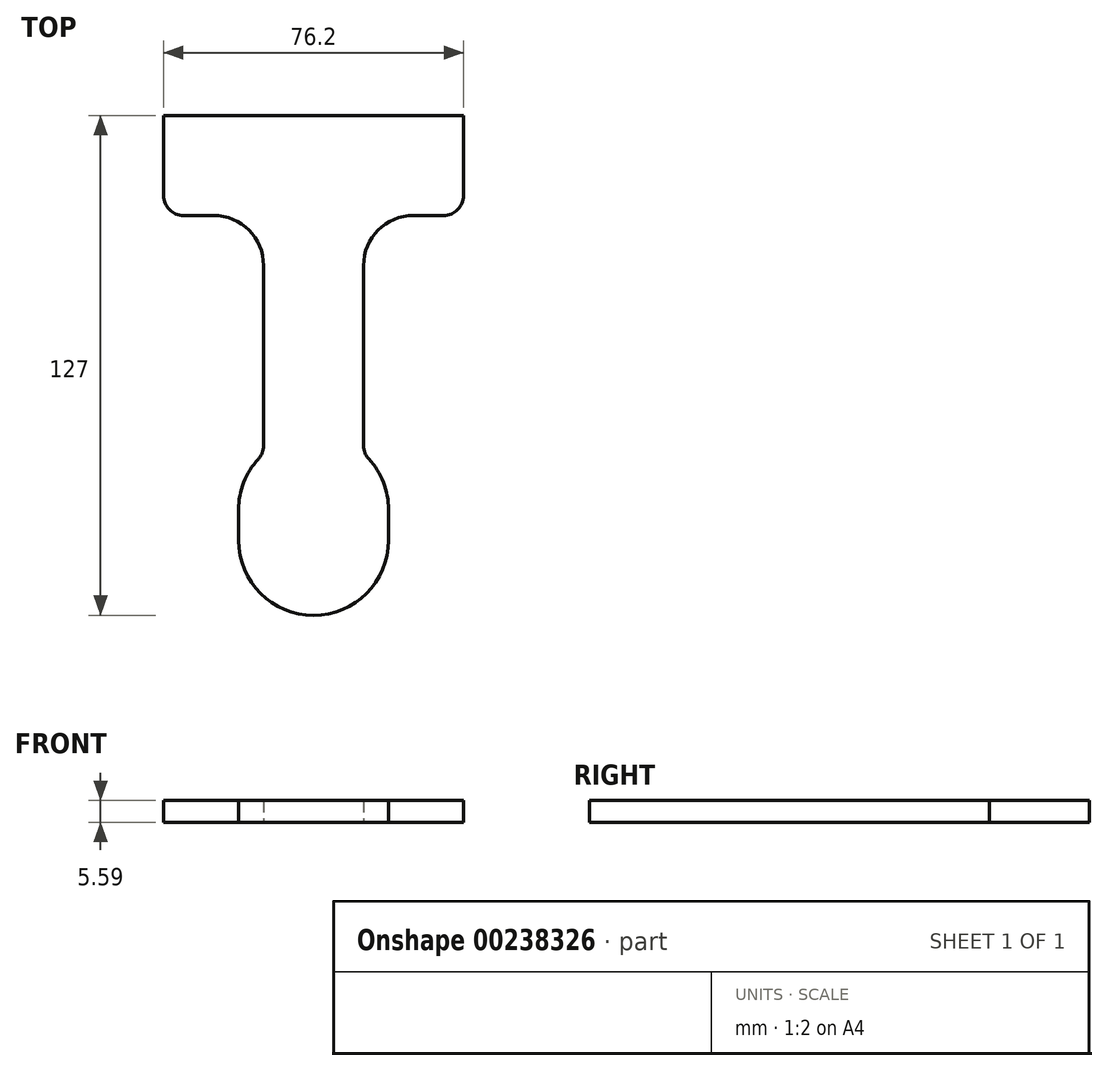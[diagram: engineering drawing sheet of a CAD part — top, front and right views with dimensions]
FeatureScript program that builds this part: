
annotation { "Feature Type Name" : "Feature", "Feature Type Description" : "" }
export const myFeature = defineFeature(function(context is Context, id is Id, definition is map)
    precondition{}
    {
        {
            var Q0;
            Q0=qCreatedBy(makeId("Top.planeOp"),FACE);
            var sketch = newSketch(context, id + "F0", { "sketchPlane" : qUnion([Q0])});
            skLineSegment(sketch, "E0.bottom", {"start": v(-38.1, 12.7) * mm, "end": v(38.1, 12.7) * mm});
            skLineSegment(sketch, "E0.top", {"start": v(-38.1, -12.7) * mm, "end": v(38.1, -12.7) * mm});
            skLineSegment(sketch, "E0.left", {"start": v(-38.1, 12.7) * mm, "end": v(-38.1, -12.7) * mm});
            skLineSegment(sketch, "E0.right", {"start": v(38.1, 12.7) * mm, "end": v(38.1, -12.7) * mm});
            skPoint(sketch, "E0.middle", {"position": v(0, 0) * mm});
            skLineSegment(sketch, "E1.bottom", {"start": v(19.05, -114.3) * mm, "end": v(-19.05, -114.3) * mm});
            skLineSegment(sketch, "E2.bottom", {"start": v(-19.05, -114.3) * mm, "end": v(19.05, -114.3) * mm});
            skLineSegment(sketch, "E2.top", {"start": v(-19.05, -76.2) * mm, "end": v(19.05, -76.2) * mm});
            skLineSegment(sketch, "E2.left", {"start": v(-19.05, -114.3) * mm, "end": v(-19.05, -76.2) * mm});
            skLineSegment(sketch, "E2.right", {"start": v(19.05, -114.3) * mm, "end": v(19.05, -76.2) * mm});
            skLineSegment(sketch, "E3.top", {"start": v(-12.7, 114.3) * mm, "end": v(12.7, 114.3) * mm});
            skLineSegment(sketch, "E4.bottom", {"start": v(-12.7, -12.7) * mm, "end": v(12.7, -12.7) * mm});
            skLineSegment(sketch, "E4.top", {"start": v(-12.7, -76.2) * mm, "end": v(12.7, -76.2) * mm});
            skLineSegment(sketch, "E4.left", {"start": v(-12.7, -12.7) * mm, "end": v(-12.7, -76.2) * mm});
            skLineSegment(sketch, "E4.right", {"start": v(12.7, -12.7) * mm, "end": v(12.7, -76.2) * mm});
            skSolve(sketch);
        }
        {
            var Q0;
            Q0=qSketchRegion(id+"F0",true);
            extrude(context, id + "F1", {"entities" : qUnion([Q0]), "depth" : 5.6 * mm});
        }
        {
            var Q0;
            Q0=makeQuery(id+"F1.opExtrude","SWEPT_EDGE",EDGE,{"disambiguationData":[OSD([sQuery(id+"F0.wireOp",EDGE,"E0.top"),sQuery(id+"F0.wireOp",EDGE,"E0.left")])]});
            var Q1;
            Q1=makeQuery(id+"F1.opExtrude","SWEPT_EDGE",EDGE,{"disambiguationData":[OSD([sQuery(id+"F0.wireOp",EDGE,"E0.top"),sQuery(id+"F0.wireOp",EDGE,"E0.right")])]});
            fillet(context, id + "F2", {"entities" : qUnion([Q0, Q1]), "radius" : 5.08 * mm, "tangentPropagation" : true, "allowEdgeOverflow" : false});
        }
        {
            var Q0;
            Q0=makeQuery(id+"F1.opExtrude","SWEPT_EDGE",EDGE,{"disambiguationData":[OSD([sQuery(id+"F0.wireOp",EDGE,"E0.top"),sQuery(id+"F0.wireOp",EDGE,"E4.bottom"),sQuery(id+"F0.wireOp",EDGE,"E4.left")])]});
            var Q1;
            Q1=makeQuery(id+"F1.opExtrude","SWEPT_EDGE",EDGE,{"disambiguationData":[OSD([sQuery(id+"F0.wireOp",EDGE,"E0.top"),sQuery(id+"F0.wireOp",EDGE,"E4.bottom"),sQuery(id+"F0.wireOp",EDGE,"E4.right")])]});
            fillet(context, id + "F3", {"entities" : qUnion([Q0, Q1]), "radius" : 12.7 * mm, "tangentPropagation" : true, "allowEdgeOverflow" : false});
        }
        {
            var Q0;
            Q0=makeQuery(id+"F1.opExtrude","SWEPT_EDGE",EDGE,{"disambiguationData":[OSD([sQuery(id+"F0.wireOp",EDGE,"E2.top"),sQuery(id+"F0.wireOp",EDGE,"E4.top"),sQuery(id+"F0.wireOp",EDGE,"E4.left")])]});
            var Q1;
            Q1=makeQuery(id+"F1.opExtrude","SWEPT_EDGE",EDGE,{"disambiguationData":[OSD([sQuery(id+"F0.wireOp",EDGE,"E2.top"),sQuery(id+"F0.wireOp",EDGE,"E4.top"),sQuery(id+"F0.wireOp",EDGE,"E4.right")])]});
            fillet(context, id + "F4", {"entities" : qUnion([Q0, Q1]), "radius" : 5.08 * mm, "tangentPropagation" : true, "allowEdgeOverflow" : false});
        }
        {
            var Q0;
            Q0=makeQuery(id+"F1.opExtrude","SWEPT_EDGE",EDGE,{"disambiguationData":[OSD([sQuery(id+"F0.wireOp",EDGE,"E2.bottom"),sQuery(id+"F0.wireOp",EDGE,"E2.left")])]});
            var Q1;
            Q1=makeQuery(id+"F1.opExtrude","SWEPT_EDGE",EDGE,{"disambiguationData":[OSD([sQuery(id+"F0.wireOp",EDGE,"E2.left"),sQuery(id+"F0.wireOp",EDGE,"E2.top")])]});
            var Q2;
            Q2=makeQuery(id+"F1.opExtrude","SWEPT_EDGE",EDGE,{"disambiguationData":[OSD([sQuery(id+"F0.wireOp",EDGE,"E2.bottom"),sQuery(id+"F0.wireOp",EDGE,"E2.right")])]});
            var Q3;
            Q3=makeQuery(id+"F1.opExtrude","SWEPT_EDGE",EDGE,{"disambiguationData":[OSD([sQuery(id+"F0.wireOp",EDGE,"E2.right"),sQuery(id+"F0.wireOp",EDGE,"E2.top")])]});
            fillet(context, id + "F5", {"entities" : qUnion([Q0, Q1, Q2, Q3]), "radius" : 19.05 * mm, "tangentPropagation" : true, "allowEdgeOverflow" : false});
        }
    });
